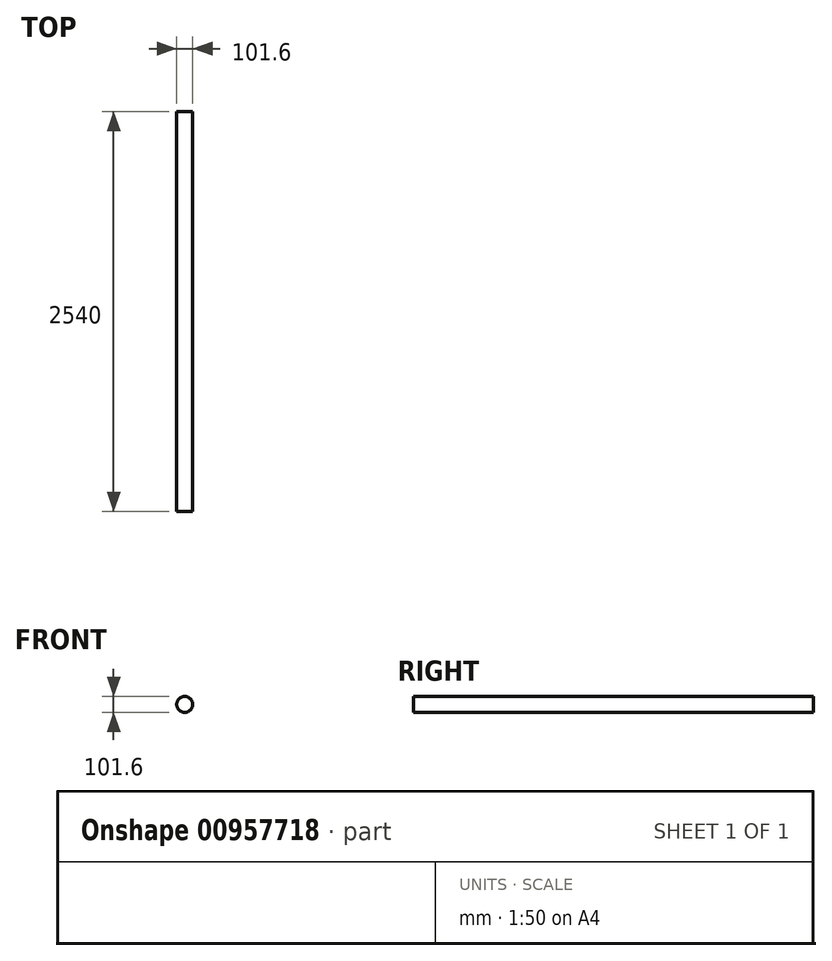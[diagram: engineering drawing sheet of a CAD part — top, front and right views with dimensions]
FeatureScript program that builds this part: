
annotation { "Feature Type Name" : "Feature", "Feature Type Description" : "" }
export const myFeature = defineFeature(function(context is Context, id is Id, definition is map)
    precondition{}
    {
        {
            var Q0;
            Q0=qCreatedBy(makeId("Front.planeOp"),FACE);
            var sketch = newSketch(context, id + "F0", { "sketchPlane" : qUnion([Q0])});
            skCircle(sketch, "E0", {"center": v(0, 0) * mm, "radius": 50.8 * mm});
            skSolve(sketch);
        }
        {
            var Q0;
            Q0=makeQuery(id+"F0.imprint","IMPRINT",FACE,{"disambiguationData":[TD([[makeQuery(id+"F0.imprint","IMPRINT",EDGE,{"derivedFrom":sQuery(id+"F0.wireOp",EDGE,"E0")}),1.0]])]});
            extrude(context, id + "F1", {"entities" : qUnion([Q0]), "depth" : 2540 * mm, "offsetDistance" : 25.4 * mm});
        }
    });
